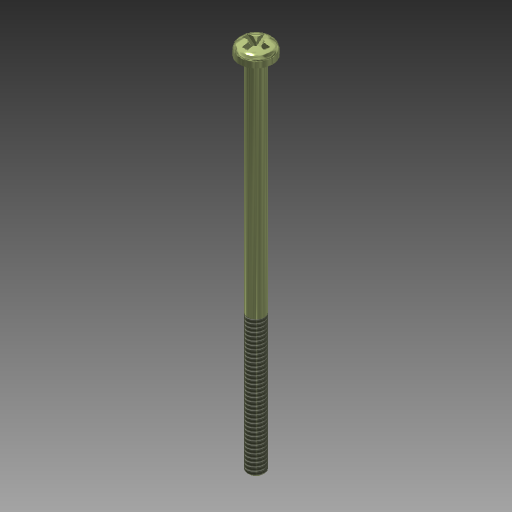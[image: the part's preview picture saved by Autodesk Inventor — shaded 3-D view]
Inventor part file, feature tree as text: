
AUTODESK INVENTOR PART (.ipt)
format: ipt  version: 2017.1 (Build 211199000, 199)  size: 115,200 bytes
history: native  units: mm
features: imported_body x1, thread x1
ambient origin geometry x8: Origin, YZ Plane, XZ Plane, XY Plane, X Axis, Y Axis, Z Axis, Center Point
bodies: Solid1 (feature_tree)
feature tree (2):
  imported_body  "Base1"
  thread  "Thread1"  [1 undecoded]
note: 1 required parameter value undecoded (feature->parameter linkage not recoverable at this tier; creation-order binding heuristic only, values carry confidence <= 0.55)
